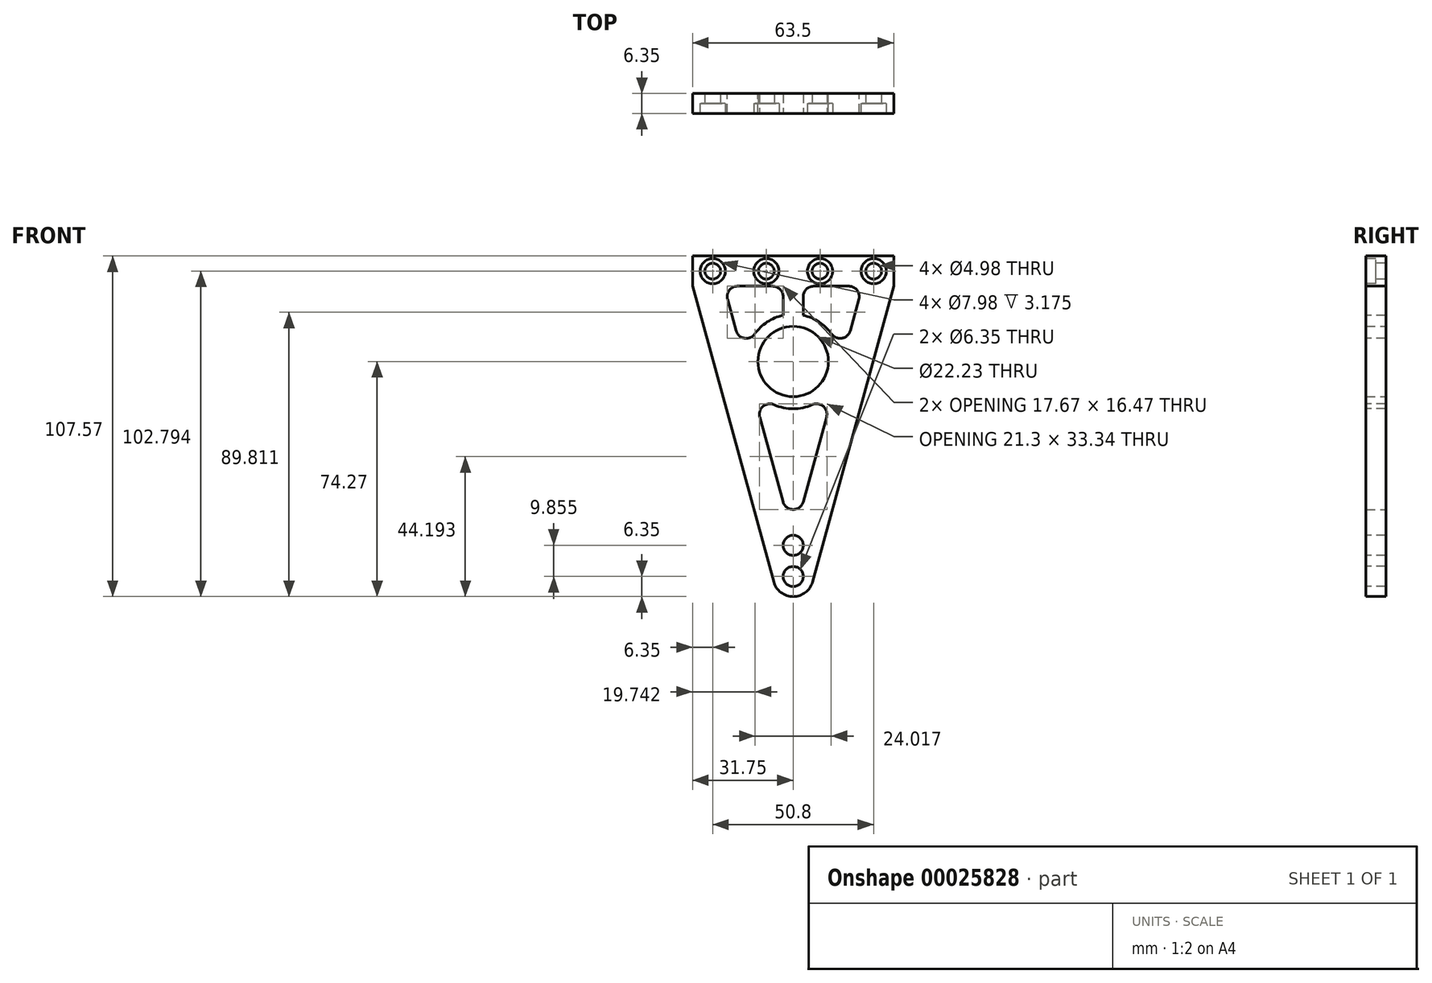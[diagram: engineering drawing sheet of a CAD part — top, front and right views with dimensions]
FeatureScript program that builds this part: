
annotation { "Feature Type Name" : "Feature", "Feature Type Description" : "" }
export const myFeature = defineFeature(function(context is Context, id is Id, definition is map)
    precondition{}
    {
        {
            var Q0;
            Q0=qCreatedBy(makeId("Front.planeOp"),FACE);
            var sketch = newSketch(context, id + "F0", { "sketchPlane" : qUnion([Q0])});
            skCircle(sketch, "E0", {"center": v(0, 0) * mm, "radius": 11.11 * mm});
            skLineSegment(sketch, "E1", {"start": v(0, 0) * mm, "end": v(0, 63.6) * mm, "construction": true});
            skLineSegment(sketch, "E2", {"start": v(0, 0) * mm, "end": v(107.94, 0) * mm, "construction": true});
            skLineSegment(sketch, "E3.bottom", {"start": v(-31.75, 33.3) * mm, "end": v(31.75, 33.3) * mm});
            skLineSegment(sketch, "E3.left", {"start": v(-31.75, 33.3) * mm, "end": v(-31.75, 23.77) * mm});
            skLineSegment(sketch, "E3.right", {"start": v(31.75, 33.3) * mm, "end": v(31.75, 23.77) * mm});
            skLineSegment(sketch, "E4", {"start": v(-31.75, 23.77) * mm, "end": v(-6.12, -69.6) * mm});
            skLineSegment(sketch, "E5", {"start": v(31.75, 23.77) * mm, "end": v(6.12, -69.6) * mm});
            skArc(sketch, "E6", {"start": v(-6.12, -69.6) * mm, "mid": v(0, -74.27) * mm, "end": v(6.12, -69.6) * mm});
            skSolve(sketch);
        }
        {
            var Q0;
            Q0=makeQuery(id+"F0.imprint","IMPRINT",FACE,{"disambiguationData":[TD([[makeQuery(id+"F0.imprint","IMPRINT",EDGE,{"derivedFrom":sQuery(id+"F0.wireOp",EDGE,"E0")}),-1.0]])]});
            extrude(context, id + "F1", {"entities" : qUnion([Q0]), "depth" : 6.35 * mm});
        }
        {
            var Q0;
            Q0=makeQuery(id+"F1.opExtrude","CAP_FACE",FACE,{"disambiguationData":[OSD([sQuery(id+"F0.wireOp",EDGE,"E0"),sQuery(id+"F0.wireOp",EDGE,"E3.bottom"),sQuery(id+"F0.wireOp",EDGE,"E3.left"),sQuery(id+"F0.wireOp",EDGE,"E3.right"),sQuery(id+"F0.wireOp",EDGE,"E4"),sQuery(id+"F0.wireOp",EDGE,"E5"),sQuery(id+"F0.wireOp",EDGE,"E6")])],"isStart":false});
            var sketch = newSketch(context, id + "F2", { "sketchPlane" : qUnion([Q0])});
            skLineSegment(sketch, "E7.0", {"start": v(21.87, 23.77) * mm, "end": v(3.17, 23.77) * mm});
            skLineSegment(sketch, "E7.2", {"start": v(0, -55.92) * mm, "end": v(13.77, -5.75) * mm});
            skLineSegment(sketch, "E7.3", {"start": v(-21.87, 23.77) * mm, "end": v(-14.78, -2.08) * mm});
            skArc(sketch, "E8", {"start": v(-13.77, -5.75) * mm, "mid": v(0, -14.92) * mm, "end": v(13.77, -5.75) * mm});
            skArc(sketch, "E9.trimOffspring", {"start": v(14.78, -2.08) * mm, "mid": v(12.25, 8.53) * mm, "end": v(3.18, 14.58) * mm});
            skLineSegment(sketch, "E10", {"start": v(0, 0) * mm, "end": v(0, 37.86) * mm, "construction": true});
            skLineSegment(sketch, "E11.trimOffspring", {"start": v(14.78, -2.08) * mm, "end": v(21.87, 23.77) * mm});
            skLineSegment(sketch, "E12.trimOffspring", {"start": v(-13.77, -5.75) * mm, "end": v(0, -55.92) * mm});
            skLineSegment(sketch, "E13", {"start": v(3.17, 23.77) * mm, "end": v(3.18, 14.58) * mm});
            skLineSegment(sketch, "E14", {"start": v(-3.17, 23.77) * mm, "end": v(-3.18, 14.58) * mm});
            skArc(sketch, "E15.trimOffspring", {"start": v(-3.18, 14.58) * mm, "mid": v(-12.25, 8.53) * mm, "end": v(-14.78, -2.08) * mm});
            skLineSegment(sketch, "E16.trimOffspring", {"start": v(-3.17, 23.77) * mm, "end": v(-21.87, 23.77) * mm});
            skSolve(sketch);
        }
        {
            var Q0;
            Q0=makeQuery(id+"F2.imprint","IMPRINT",FACE,{"disambiguationData":[TD([[makeQuery(id+"F2.imprint","IMPRINT",EDGE,{"derivedFrom":sQuery(id+"F2.wireOp",EDGE,"E7.3")}),1.0]])]});
            var Q1;
            Q1=makeQuery(id+"F2.imprint","IMPRINT",FACE,{"disambiguationData":[TD([[makeQuery(id+"F2.imprint","IMPRINT",EDGE,{"derivedFrom":sQuery(id+"F2.wireOp",EDGE,"E7.0")}),1.0]])]});
            var Q2;
            Q2=makeQuery(id+"F2.imprint","IMPRINT",FACE,{"disambiguationData":[TD([[makeQuery(id+"F2.imprint","IMPRINT",EDGE,{"derivedFrom":sQuery(id+"F2.wireOp",EDGE,"E7.2")}),1.0]])]});
            extrude(context, id + "F3", {"entities" : qUnion([Q0, Q1, Q2]), "operationType" : NewBodyOperationType.REMOVE, "oppositeDirection" : true, "depth" : 6.35 * mm});
        }
        {
            var Q0;
            Q0=makeQuery(id+"F3.boolean.opBoolean","COPY",EDGE,{"derivedFrom":makeQuery(id+"F3.opExtrude","SWEPT_EDGE",EDGE,{"disambiguationData":[OSD([sQuery(id+"F2.wireOp",EDGE,"E7.3"),sQuery(id+"F2.wireOp",EDGE,"E15.trimOffspring")])]})});
            var Q1;
            Q1=makeQuery(id+"F3.boolean.opBoolean","COPY",EDGE,{"derivedFrom":makeQuery(id+"F3.opExtrude","SWEPT_EDGE",EDGE,{"disambiguationData":[OSD([sQuery(id+"F2.wireOp",EDGE,"E9.trimOffspring"),sQuery(id+"F2.wireOp",EDGE,"E11.trimOffspring")])]})});
            var Q2;
            Q2=makeQuery(id+"F3.boolean.opBoolean","COPY",EDGE,{"derivedFrom":makeQuery(id+"F3.opExtrude","SWEPT_EDGE",EDGE,{"disambiguationData":[OSD([sQuery(id+"F2.wireOp",EDGE,"E7.0"),sQuery(id+"F2.wireOp",EDGE,"E13")])]})});
            var Q3;
            Q3=makeQuery(id+"F3.boolean.opBoolean","COPY",EDGE,{"derivedFrom":makeQuery(id+"F3.opExtrude","SWEPT_EDGE",EDGE,{"disambiguationData":[OSD([sQuery(id+"F2.wireOp",EDGE,"E7.0"),sQuery(id+"F2.wireOp",EDGE,"E11.trimOffspring")])]})});
            var Q4;
            Q4=makeQuery(id+"F3.boolean.opBoolean","COPY",EDGE,{"derivedFrom":makeQuery(id+"F3.opExtrude","SWEPT_EDGE",EDGE,{"disambiguationData":[OSD([sQuery(id+"F2.wireOp",EDGE,"E14"),sQuery(id+"F2.wireOp",EDGE,"E16.trimOffspring")])]})});
            var Q5;
            Q5=makeQuery(id+"F3.boolean.opBoolean","COPY",EDGE,{"derivedFrom":makeQuery(id+"F3.opExtrude","SWEPT_EDGE",EDGE,{"disambiguationData":[OSD([sQuery(id+"F2.wireOp",EDGE,"E7.3"),sQuery(id+"F2.wireOp",EDGE,"E16.trimOffspring")])]})});
            var Q6;
            Q6=makeQuery(id+"F3.boolean.opBoolean","COPY",EDGE,{"derivedFrom":makeQuery(id+"F3.opExtrude","SWEPT_EDGE",EDGE,{"disambiguationData":[OSD([sQuery(id+"F2.wireOp",EDGE,"E7.2"),sQuery(id+"F2.wireOp",EDGE,"E12.trimOffspring")])]})});
            var Q7;
            Q7=makeQuery(id+"F3.boolean.opBoolean","COPY",EDGE,{"derivedFrom":makeQuery(id+"F3.opExtrude","SWEPT_EDGE",EDGE,{"disambiguationData":[OSD([sQuery(id+"F2.wireOp",EDGE,"E8"),sQuery(id+"F2.wireOp",EDGE,"E12.trimOffspring")])]})});
            var Q8;
            Q8=makeQuery(id+"F3.boolean.opBoolean","COPY",EDGE,{"derivedFrom":makeQuery(id+"F3.opExtrude","SWEPT_EDGE",EDGE,{"disambiguationData":[OSD([sQuery(id+"F2.wireOp",EDGE,"E7.2"),sQuery(id+"F2.wireOp",EDGE,"E8")])]})});
            fillet(context, id + "F4", {"entities" : qUnion([Q0, Q1, Q2, Q3, Q4, Q5, Q6, Q7, Q8]), "radius" : 3.3 * mm, "tangentPropagation" : true, "allowEdgeOverflow" : false});
        }
        {
            var Q0;
            Q0=makeQuery(id+"F1.opExtrude","CAP_FACE",FACE,{"disambiguationData":[OSD([sQuery(id+"F0.wireOp",EDGE,"E0"),sQuery(id+"F0.wireOp",EDGE,"E3.bottom"),sQuery(id+"F0.wireOp",EDGE,"E3.left"),sQuery(id+"F0.wireOp",EDGE,"E3.right"),sQuery(id+"F0.wireOp",EDGE,"E4"),sQuery(id+"F0.wireOp",EDGE,"E5"),sQuery(id+"F0.wireOp",EDGE,"E6")])],"isStart":false});
            var sketch = newSketch(context, id + "F5", { "sketchPlane" : qUnion([Q0])});
            skLineSegment(sketch, "E17", {"start": v(0, 33.3) * mm, "end": v(0, -74.27) * mm});
            skLineSegment(sketch, "E18", {"start": v(-25.4, 28.52) * mm, "end": v(25.4, 28.52) * mm});
            skPoint(sketch, "E19", {"position": v(-25.4, 28.52) * mm});
            skPoint(sketch, "E20", {"position": v(-8.47, 28.52) * mm});
            skPoint(sketch, "E21", {"position": v(8.47, 28.52) * mm});
            skPoint(sketch, "E22", {"position": v(25.4, 28.52) * mm});
            skPoint(sketch, "E23", {"position": v(0, -58.06) * mm});
            skPoint(sketch, "E24", {"position": v(0, -67.92) * mm});
            skSolve(sketch);
        }
        {
            var Q0;
            Q0=sQuery(id+"F5.wireOp",VERTEX,"E19");
            var Q1;
            Q1=sQuery(id+"F5.wireOp",VERTEX,"E20");
            var Q2;
            Q2=sQuery(id+"F5.wireOp",VERTEX,"E21");
            var Q3;
            Q3=sQuery(id+"F5.wireOp",VERTEX,"E22");
            var Q4;
            Q4=makeQuery(id+"F1.opExtrude","SWEPT_BODY",BODY,{"disambiguationData":[OSD([sQuery(id+"F0.wireOp",EDGE,"E0"),sQuery(id+"F0.wireOp",EDGE,"E3.bottom"),sQuery(id+"F0.wireOp",EDGE,"E3.left"),sQuery(id+"F0.wireOp",EDGE,"E3.right"),sQuery(id+"F0.wireOp",EDGE,"E4"),sQuery(id+"F0.wireOp",EDGE,"E5"),sQuery(id+"F0.wireOp",EDGE,"E6")])]});
            hole(context, id + "F6", {"style" : HoleStyle.C_BORE, "holeDiameter" : 4.98 * mm, "cBoreDiameter" : 7.98 * mm, "cBoreDepth" : 3.17 * mm, "endStyle" : HoleEndStyle.THROUGH, "locations" : qUnion([Q0, Q1, Q2, Q3]), "scope" : qUnion([Q4])});
        }
        {
            var Q0;
            Q0=sQuery(id+"F5.wireOp",VERTEX,"E23");
            var Q1;
            Q1=sQuery(id+"F5.wireOp",VERTEX,"E24");
            var Q2;
            Q2=makeQuery(id+"F1.opExtrude","SWEPT_BODY",BODY,{"disambiguationData":[OSD([sQuery(id+"F0.wireOp",EDGE,"E0"),sQuery(id+"F0.wireOp",EDGE,"E3.bottom"),sQuery(id+"F0.wireOp",EDGE,"E3.left"),sQuery(id+"F0.wireOp",EDGE,"E3.right"),sQuery(id+"F0.wireOp",EDGE,"E4"),sQuery(id+"F0.wireOp",EDGE,"E5"),sQuery(id+"F0.wireOp",EDGE,"E6")])]});
            hole(context, id + "F7", {"style" : HoleStyle.SIMPLE, "holeDiameter" : 6.35 * mm, "endStyle" : HoleEndStyle.THROUGH, "locations" : qUnion([Q0, Q1]), "scope" : qUnion([Q2])});
        }
    });
